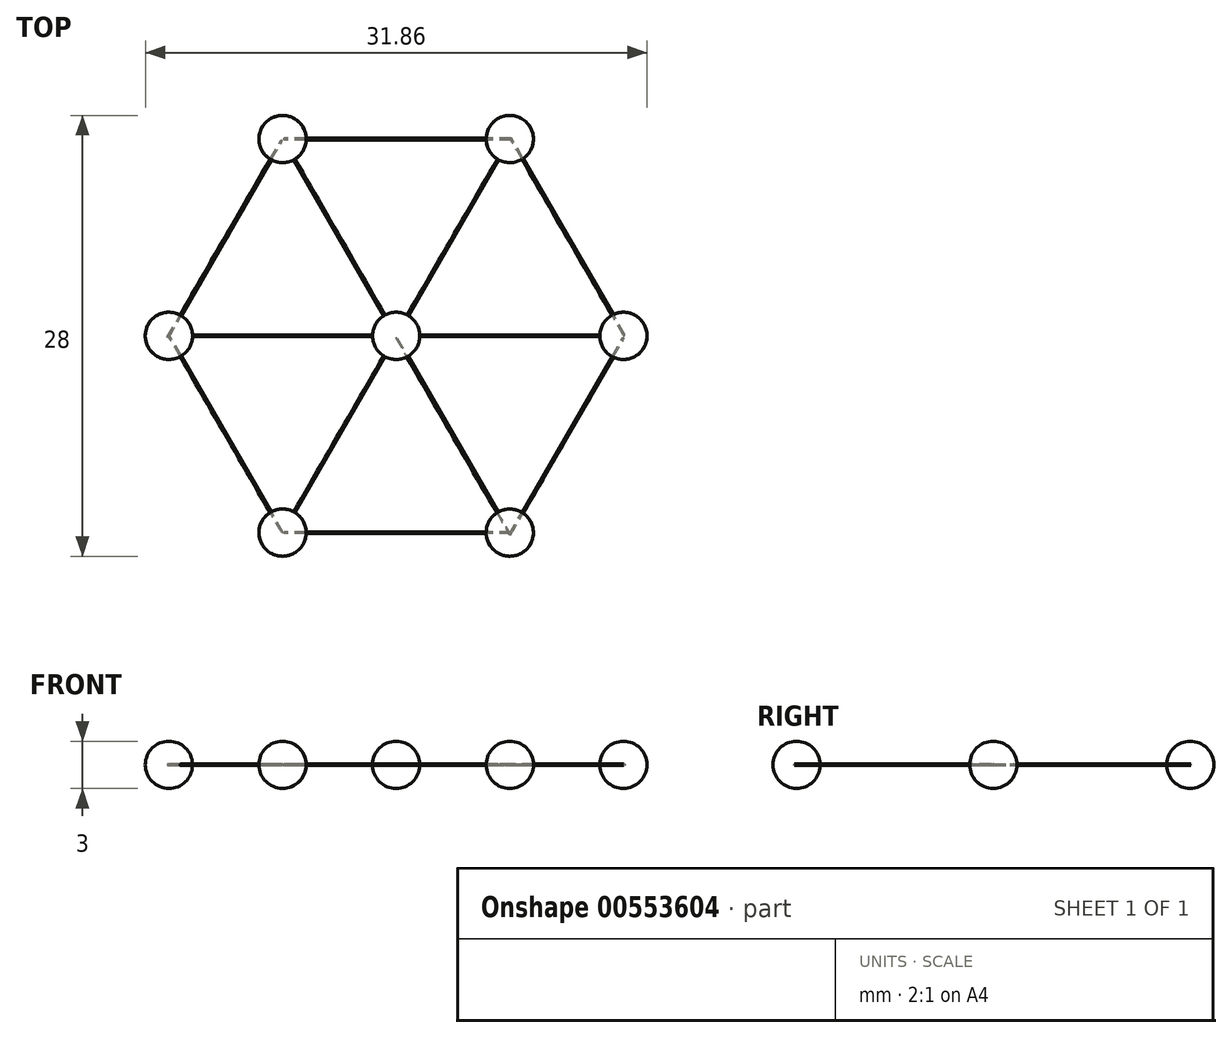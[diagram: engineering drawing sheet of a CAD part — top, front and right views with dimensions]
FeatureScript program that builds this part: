
annotation { "Feature Type Name" : "Feature", "Feature Type Description" : "" }
export const myFeature = defineFeature(function(context is Context, id is Id, definition is map)
    precondition{}
    {
        {
            var Q0;
            Q0=qCreatedBy(makeId("Top.planeOp"),FACE);
            var sketch = newSketch(context, id + "F0", { "sketchPlane" : qUnion([Q0])});
            skArc(sketch, "E0", {"start": v(0, -1.5) * mm, "mid": v(1.5, 0) * mm, "end": v(0, 1.5) * mm});
            skLineSegment(sketch, "E1", {"start": v(0, 1.5) * mm, "end": v(0, -1.5) * mm});
            skSolve(sketch);
        }
        {
            var Q0;
            Q0 = qSketchRegion(id + "F0", true);
            var Q1;
            Q1=sQuery(id+"F0.wireOp",EDGE,"E1");
            revolve(context, id + "F1", {"entities" : qUnion([Q0]), "axis" : qUnion([Q1]), "revolveType" : RevolveType.FULL});
        }
        {
            var Q0;
            Q0=qCreatedBy(makeId("Top.planeOp"),FACE);
            var sketch = newSketch(context, id + "F2", { "sketchPlane" : qUnion([Q0])});
            skCircle(sketch, "E2.cCircle", {"center": v(0, 0) * mm, "radius": 12.5 * mm, "construction": true});
            skLineSegment(sketch, "E2.0", {"start": v(7.22, 12.5) * mm, "end": v(14.43, 0) * mm});
            skLineSegment(sketch, "E2.1", {"start": v(14.43, 0) * mm, "end": v(7.22, -12.5) * mm});
            skLineSegment(sketch, "E2.2", {"start": v(7.22, -12.5) * mm, "end": v(-7.22, -12.5) * mm});
            skLineSegment(sketch, "E2.3", {"start": v(-7.22, -12.5) * mm, "end": v(-14.43, 0) * mm});
            skLineSegment(sketch, "E2.4", {"start": v(-14.43, 0) * mm, "end": v(-7.22, 12.5) * mm});
            skLineSegment(sketch, "E2.5", {"start": v(-7.22, 12.5) * mm, "end": v(7.22, 12.5) * mm});
            skPoint(sketch, "E2.0.midPoint", {"position": v(10.83, 6.25) * mm});
            skLineSegment(sketch, "E3", {"start": v(0, 0) * mm, "end": v(7.22, 12.5) * mm});
            skLineSegment(sketch, "E4", {"start": v(0, 0) * mm, "end": v(-7.22, 12.5) * mm});
            skLineSegment(sketch, "E5", {"start": v(0, 0) * mm, "end": v(-14.43, 0) * mm});
            skLineSegment(sketch, "E6", {"start": v(0, 0) * mm, "end": v(-7.22, -12.5) * mm});
            skLineSegment(sketch, "E7", {"start": v(0, 0) * mm, "end": v(7.22, -12.5) * mm});
            skLineSegment(sketch, "E8", {"start": v(0, 0) * mm, "end": v(14.43, 0) * mm});
            skSolve(sketch);
        }
        {
            var Q0;
            Q0=sQuery(id+"F2.wireOp",VERTEX,"E2.3.start");
            var Q1;
            Q1=sQuery(id+"F2.wireOp",EDGE,"E6");
            cPlane(context, id + "F3", {"entities" : qUnion([Q0, Q1]), "cplaneType" : CPlaneType.LINE_POINT, "offset" : 25 * mm, "width" : 150 * mm, "height" : 150 * mm});
        }
        {
            var Q0;
            Q0=sQuery(id+"F2.wireOp",VERTEX,"E5.end");
            var Q1;
            Q1=sQuery(id+"F2.wireOp",EDGE,"E5");
            cPlane(context, id + "F4", {"entities" : qUnion([Q0, Q1]), "cplaneType" : CPlaneType.LINE_POINT, "offset" : 25 * mm, "width" : 150 * mm, "height" : 150 * mm});
        }
        {
            var Q0;
            Q0=sQuery(id+"F2.wireOp",VERTEX,"E4.end");
            var Q1;
            Q1=sQuery(id+"F2.wireOp",EDGE,"E4");
            cPlane(context, id + "F5", {"entities" : qUnion([Q0, Q1]), "cplaneType" : CPlaneType.LINE_POINT, "offset" : 25 * mm, "width" : 150 * mm, "height" : 150 * mm});
        }
        {
            var Q0;
            Q0=qCreatedBy(id+"F3.planeOp",FACE);
            var sketch = newSketch(context, id + "F6", { "sketchPlane" : qUnion([Q0])});
            skCircle(sketch, "E9", {"center": v(0, 0) * mm, "radius": 0.05 * mm});
            skSolve(sketch);
        }
        {
            var Q0;
            Q0=qCreatedBy(id+"F4.planeOp",FACE);
            var sketch = newSketch(context, id + "F7", { "sketchPlane" : qUnion([Q0])});
            skCircle(sketch, "E10", {"center": v(0, 0) * mm, "radius": 0.05 * mm});
            skSolve(sketch);
        }
        {
            var Q0;
            Q0=qCreatedBy(id+"F5.planeOp",FACE);
            var sketch = newSketch(context, id + "F8", { "sketchPlane" : qUnion([Q0])});
            skCircle(sketch, "E11", {"center": v(0, 0) * mm, "radius": 0.05 * mm});
            skSolve(sketch);
        }
        {
            var Q0;
            Q0=makeQuery(id+"F8.imprint","IMPRINT",FACE,{"disambiguationData":[TD([[makeQuery(id+"F8.imprint","IMPRINT",EDGE,{"derivedFrom":sQuery(id+"F8.wireOp",EDGE,"E11")}),1.0]])]});
            var Q1;
            Q1=sQuery(id+"F2.wireOp",EDGE,"E4");
            var Q2;
            Q2=sQuery(id+"F2.wireOp",EDGE,"E7");
            sweep(context, id + "F9", {"operationType" : NewBodyOperationType.ADD, "profiles" : qUnion([Q0]), "path" : qUnion([Q1, Q2])});
        }
        {
            var Q0;
            Q0=makeQuery(id+"F7.imprint","IMPRINT",FACE,{"disambiguationData":[TD([[makeQuery(id+"F7.imprint","IMPRINT",EDGE,{"derivedFrom":sQuery(id+"F7.wireOp",EDGE,"E10")}),1.0]])]});
            var Q1;
            Q1=sQuery(id+"F2.wireOp",EDGE,"E5");
            var Q2;
            Q2=sQuery(id+"F2.wireOp",EDGE,"E8");
            sweep(context, id + "F10", {"operationType" : NewBodyOperationType.ADD, "profiles" : qUnion([Q0]), "path" : qUnion([Q1, Q2])});
        }
        {
            var Q0;
            Q0=makeQuery(id+"F6.imprint","IMPRINT",FACE,{"disambiguationData":[TD([[makeQuery(id+"F6.imprint","IMPRINT",EDGE,{"derivedFrom":sQuery(id+"F6.wireOp",EDGE,"E9")}),1.0]])]});
            var Q1;
            Q1=sQuery(id+"F2.wireOp",EDGE,"E6");
            var Q2;
            Q2=sQuery(id+"F2.wireOp",EDGE,"E3");
            sweep(context, id + "F11", {"operationType" : NewBodyOperationType.ADD, "profiles" : qUnion([Q0]), "path" : qUnion([Q1, Q2])});
        }
        {
            var Q0;
            Q0=qCreatedBy(id+"F3.planeOp",FACE);
            var sketch = newSketch(context, id + "F12", { "sketchPlane" : qUnion([Q0])});
            skArc(sketch, "E12", {"start": v(0, -1.5) * mm, "mid": v(1.5, 0) * mm, "end": v(0, 1.5) * mm});
            skLineSegment(sketch, "E13", {"start": v(0, 1.5) * mm, "end": v(0, -1.5) * mm});
            skSolve(sketch);
        }
        {
            var Q0;
            Q0 = qSketchRegion(id + "F12", true);
            var Q1;
            Q1=sQuery(id+"F12.wireOp",EDGE,"E13");
            revolve(context, id + "F13", {"entities" : qUnion([Q0]), "axis" : qUnion([Q1]), "revolveType" : RevolveType.FULL});
        }
        {
            var Q0;
            Q0=makeQuery(id+"F13.opRevolve","SWEPT_BODY",BODY,{"disambiguationData":[OSD([sQuery(id+"F12.wireOp",EDGE,"E12"),sQuery(id+"F12.wireOp",EDGE,"E13")])]});
            var Q1;
            Q1=sQuery(id+"F2.wireOp",EDGE,"E2.cCircle");
            circularPattern(context, id + "F14", {"entities" : qUnion([Q0]), "axis" : qUnion([Q1]), "angle" : 360 * degree, "instanceCount" : 6, "equalSpace" : true});
        }
        {
            var Q0;
            Q0=qCreatedBy(makeId("Right.planeOp"),FACE);
            cPlane(context, id + "F15", {"entities" : qUnion([Q0]), "cplaneType" : CPlaneType.OFFSET, "offset" : 7.3 * mm, "width" : 150 * mm, "height" : 150 * mm});
        }
        {
            var Q0;
            Q0=qCreatedBy(id+"F15.planeOp",FACE);
            var sketch = newSketch(context, id + "F16", { "sketchPlane" : qUnion([Q0])});
            skPoint(sketch, "E14.0", {"position": v(-12.5, 0) * mm});
            skPoint(sketch, "E15.0", {"position": v(12.5, 0) * mm});
            skCircle(sketch, "E16", {"center": v(-12.5, 0) * mm, "radius": 0.05 * mm});
            skCircle(sketch, "E17", {"center": v(12.5, 0) * mm, "radius": 0.05 * mm});
            skSolve(sketch);
        }
        {
            var Q0;
            Q0=makeQuery(id+"F16.imprint","IMPRINT",FACE,{"disambiguationData":[TD([[makeQuery(id+"F16.imprint","IMPRINT",EDGE,{"derivedFrom":sQuery(id+"F16.wireOp",EDGE,"E16")}),1.0]])]});
            var Q1;
            Q1=sQuery(id+"F2.wireOp",EDGE,"E2.2");
            sweep(context, id + "F17", {"profiles" : qUnion([Q0]), "path" : qUnion([Q1])});
        }
        {
            var Q0;
            Q0=makeQuery(id+"F16.imprint","IMPRINT",FACE,{"disambiguationData":[TD([[makeQuery(id+"F16.imprint","IMPRINT",EDGE,{"derivedFrom":sQuery(id+"F16.wireOp",EDGE,"E17")}),1.0]])]});
            var Q1;
            Q1=sQuery(id+"F2.wireOp",EDGE,"E2.5");
            sweep(context, id + "F18", {"profiles" : qUnion([Q0]), "path" : qUnion([Q1])});
        }
        {
            var Q0;
            Q0=qCreatedBy(id+"F3.planeOp",FACE);
            cPlane(context, id + "F19", {"entities" : qUnion([Q0]), "cplaneType" : CPlaneType.OFFSET, "offset" : 7.1 * mm, "oppositeDirection" : true, "width" : 150 * mm, "height" : 150 * mm});
        }
        {
            var Q0;
            Q0=qCreatedBy(id+"F19.planeOp",FACE);
            var sketch = newSketch(context, id + "F20", { "sketchPlane" : qUnion([Q0])});
            skPoint(sketch, "E18.0", {"position": v(-12.5, 0) * mm});
            skPoint(sketch, "E19.0", {"position": v(12.57, 0) * mm});
            skCircle(sketch, "E20", {"center": v(-12.5, 0) * mm, "radius": 0.05 * mm});
            skCircle(sketch, "E21", {"center": v(12.57, 0) * mm, "radius": 0.05 * mm});
            skSolve(sketch);
        }
        {
            var Q0;
            Q0=makeQuery(id+"F20.imprint","IMPRINT",FACE,{"disambiguationData":[TD([[makeQuery(id+"F20.imprint","IMPRINT",EDGE,{"derivedFrom":sQuery(id+"F20.wireOp",EDGE,"E21")}),1.0]])]});
            var Q1;
            Q1=sQuery(id+"F2.wireOp",EDGE,"E2.1");
            sweep(context, id + "F21", {"profiles" : qUnion([Q0]), "path" : qUnion([Q1])});
        }
        {
            var Q0;
            Q0=makeQuery(id+"F20.imprint","IMPRINT",FACE,{"disambiguationData":[TD([[makeQuery(id+"F20.imprint","IMPRINT",EDGE,{"derivedFrom":sQuery(id+"F20.wireOp",EDGE,"E20")}),1.0]])]});
            var Q1;
            Q1=sQuery(id+"F2.wireOp",EDGE,"E2.4");
            sweep(context, id + "F22", {"profiles" : qUnion([Q0]), "path" : qUnion([Q1])});
        }
        {
            var Q0;
            Q0=sQuery(id+"F2.wireOp",VERTEX,"E2.3.start");
            var Q1;
            Q1=sQuery(id+"F2.wireOp",EDGE,"E2.3");
            cPlane(context, id + "F23", {"entities" : qUnion([Q0, Q1]), "cplaneType" : CPlaneType.LINE_POINT, "offset" : 25 * mm, "width" : 150 * mm, "height" : 150 * mm});
        }
        {
            var Q0;
            Q0=qCreatedBy(id+"F23.planeOp",FACE);
            var sketch = newSketch(context, id + "F24", { "sketchPlane" : qUnion([Q0])});
            skPoint(sketch, "E22.0", {"position": v(12.5, 0) * mm});
            skPoint(sketch, "E23.0", {"position": v(0.07, 0) * mm});
            skCircle(sketch, "E24", {"center": v(12.5, 0) * mm, "radius": 0.05 * mm});
            skPoint(sketch, "E25.0", {"position": v(-12.57, 0) * mm});
            skCircle(sketch, "E26", {"center": v(-12.57, 0) * mm, "radius": 0.05 * mm});
            skSolve(sketch);
        }
        {
            var Q0;
            Q0=makeQuery(id+"F24.imprint","IMPRINT",FACE,{"disambiguationData":[TD([[makeQuery(id+"F24.imprint","IMPRINT",EDGE,{"derivedFrom":sQuery(id+"F24.wireOp",EDGE,"E24")}),1.0]])]});
            var Q1;
            Q1=sQuery(id+"F2.wireOp",EDGE,"E2.3");
            sweep(context, id + "F25", {"profiles" : qUnion([Q0]), "path" : qUnion([Q1])});
        }
        {
            var Q0;
            Q0=makeQuery(id+"F20.imprint","IMPRINT",FACE,{"disambiguationData":[TD([[makeQuery(id+"F20.imprint","IMPRINT",EDGE,{"derivedFrom":sQuery(id+"F20.wireOp",EDGE,"E21")}),1.0]])]});
            var Q1;
            Q1=sQuery(id+"F2.wireOp",EDGE,"E2.0");
            sweep(context, id + "F26", {"profiles" : qUnion([Q0]), "path" : qUnion([Q1])});
        }
        {
            var Q0;
            Q0=makeQuery(id+"F24.imprint","IMPRINT",FACE,{"disambiguationData":[TD([[makeQuery(id+"F24.imprint","IMPRINT",EDGE,{"derivedFrom":sQuery(id+"F24.wireOp",EDGE,"E26")}),1.0]])]});
            var Q1;
            Q1=sQuery(id+"F2.wireOp",EDGE,"E2.0");
            sweep(context, id + "F27", {"profiles" : qUnion([Q0]), "path" : qUnion([Q1])});
        }
    });
